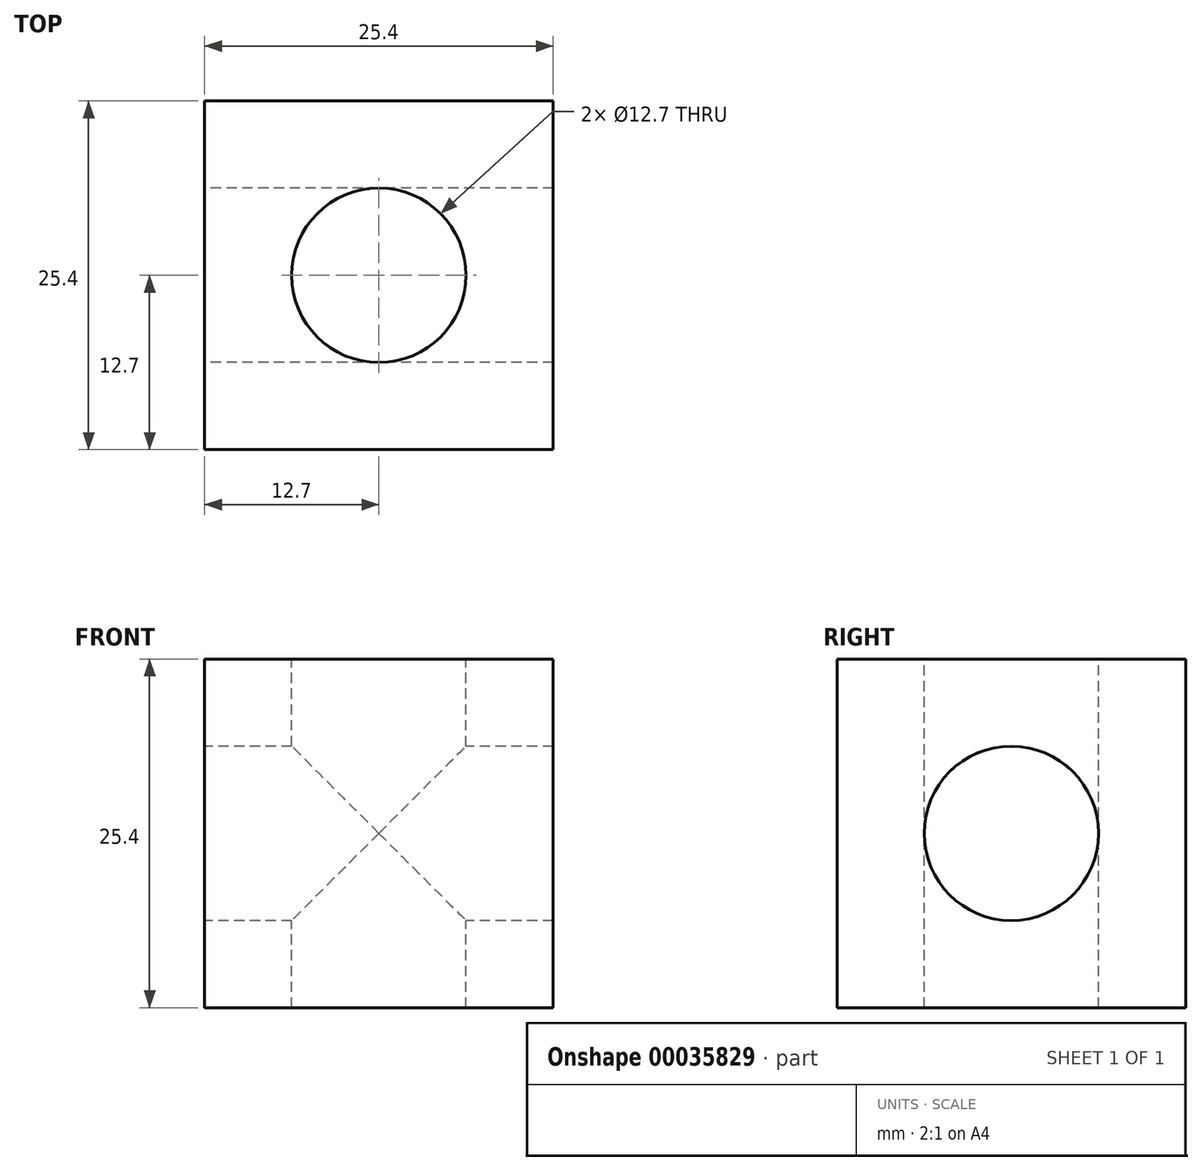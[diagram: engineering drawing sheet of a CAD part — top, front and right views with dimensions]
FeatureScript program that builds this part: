
annotation { "Feature Type Name" : "Feature", "Feature Type Description" : "" }
export const myFeature = defineFeature(function(context is Context, id is Id, definition is map)
    precondition{}
    {
        {
            var Q0;
            Q0=qCreatedBy(makeId("Right.planeOp"),FACE);
            var sketch = newSketch(context, id + "F0", { "sketchPlane" : qUnion([Q0])});
            skLineSegment(sketch, "E0", {"start": v(-25.4, 25.4) * mm, "end": v(-25.4, 0) * mm});
            skLineSegment(sketch, "E1", {"start": v(-25.4, 0) * mm, "end": v(0, 0) * mm});
            skLineSegment(sketch, "E2", {"start": v(0, 0) * mm, "end": v(0, 25.4) * mm});
            skLineSegment(sketch, "E3", {"start": v(0, 25.4) * mm, "end": v(-25.4, 25.4) * mm});
            skCircle(sketch, "E4", {"center": v(-12.7, 12.7) * mm, "radius": 6.35 * mm});
            skSolve(sketch);
        }
        {
            var Q0;
            Q0=makeQuery(id+"F0.imprint","IMPRINT",FACE,{"disambiguationData":[TD([[makeQuery(id+"F0.imprint","IMPRINT",EDGE,{"derivedFrom":sQuery(id+"F0.wireOp",EDGE,"E0")}),1.0]])]});
            extrude(context, id + "F1", {"entities" : qUnion([Q0]), "depth" : 25.4 * mm});
        }
        {
            var Q0;
            Q0=makeQuery(id+"F1.opExtrude","SWEPT_FACE",FACE,{"disambiguationData":[OSD([sQuery(id+"F0.wireOp",EDGE,"E3")])]});
            var sketch = newSketch(context, id + "F2", { "sketchPlane" : qUnion([Q0])});
            skCircle(sketch, "E5", {"center": v(12.7, -12.7) * mm, "radius": 6.35 * mm});
            skSolve(sketch);
        }
        {
            var Q0;
            Q0=makeQuery(id+"F2.imprint","IMPRINT",FACE,{"disambiguationData":[TD([[makeQuery(id+"F2.imprint","IMPRINT",EDGE,{"derivedFrom":sQuery(id+"F2.wireOp",EDGE,"E5")}),1.0]])]});
            extrude(context, id + "F3", {"entities" : qUnion([Q0]), "operationType" : NewBodyOperationType.REMOVE, "endBound" : BoundingType.THROUGH_ALL, "oppositeDirection" : true, "depth" : 25.4 * mm});
        }
    });
